# Revit family: SE-SU-600_GENERADO
name_source: partatom
category: Equipos especializados
revit_build: Autodesk Revit 2014 (Build: 20130308_1515(x64)
units: mm (PartAtom-declared; Revit-internal decimal feet)

## types (32) — shared parameters
Depth = 566 mm  [stored 1.85696 ft]
Fabricante = SAMMIC S.L.
Foodservice Equipment Identifier = Sí
Height = 997 mm  [stored 3.271 ft]
Revision Code = 1
URL = https://www.sammic.com
URL Cutsheet = http://www.sammic.com
Width = 740 mm  [stored 2.42782 ft]

## per-type parameters (varying)
| type | Comentarios de tipo | Cycle | FL Amps | HP | Modelo | Phase | Specification by Manufacturer | Volts | Watts | Weight in Pounds |
| Vacuum packing machine SE-604 230-400/50/3N | Floorstanding unit. 40 m³/h. 413+656 mm.

ELECTRICAL DATA:

230V/50Hz/3~ (8.8A) | 50 Hz | 5 A | 3.49 | 1140650 | 3 | Two sealing bars (413+656 mm.)
40 m³/h Busch vacuum pump.
Vacuum controlled by sensor. | 400 V | 2600 W | 319.7 |
| Vacuum packing machine SE-604 208-240V/60/3 | Floorstanding unit. 40 m³/h. 413+656 mm.

ELECTRICAL DATA:

230V/60Hz/3~ (7.4A) | 60 Hz | 7 A | 4.29 | 1140656 | 3 | Two sealing bars (413+656 mm.)
40 m³/h Busch vacuum pump.
Vacuum controlled by sensor. | 208 V | 3200 W | 319.7 |
| Vacuum packing machine SE-604 380/60/3N | Floorstanding unit. 40 m³/h. 413+656 mm. | 60 Hz | 5 A | 3.49 | 1140660 | 3 | Two sealing bars (413+656 mm.)
40 m³/h Busch vacuum pump.
Vacuum controlled by sensor. | 380 V | 2600 W | 319.7 |
| Vacuum packing machine SE-604 CC 230-400/50/3N | Floorstanding unit. 40m³/h. 465+465 mm.

ELECTRICAL DATA:

230V/50Hz/3~ (8.8A) | 50 Hz | 5 A | 3.08 | 1140651 | 3 | Two sealing bars (465+465 mm.)
40 m³/h Busch vacuum pump.
Vacuum controlled by sensor. | 400 V | 2300 W | 319.7 |
| Vacuum packing machine SE-604 CC 208-240V/60/3 | Floorstanding unit. 40m³/h. 465+465 mm.

ELECTRICAL DATA:

230V/60Hz/3~ (7.4A) | 60 Hz | 7 A | 3.89 | 1140657 | 3 | Two sealing bars (465+465 mm.)
40 m³/h Busch vacuum pump.
Vacuum controlled by sensor. | 208 V | 2900 W | 319.7 |
| Vacuum packing machine SE-606 230-400/50/3N | Floorstanding unit. 63 m³/h. 413+656 mm.

ELECTRICAL DATA:

230V/50Hz/3~ (9.5A) | 50 Hz | 6 A | 4.02 | 1140662 | 3 | Two sealing bars (413+656 mm.)
63 m³/h Busch vacuum pump.
Vacuum controlled by sensor. | 400 V | 3000 W | 350.5 |
| Vacuum packing machine SE-606 208-240V/60/3 | Floorstanding unit. 63 m³/h. 413+656 mm.

ELECTRICAL DATA:

230V/60Hz/3~ (8.2A) | 60 Hz | 8 A | 5.23 | 1140668 | 3 | Two sealing bars (413+656 mm.)
63 m³/h Busch vacuum pump.
Vacuum controlled by sensor. | 208 V | 3900 W | 350.5 |
| Vacuum packing machine SE-606 230V/50/1 | Floorstanding unit. 63 m³/h. 413+656 mm. | 50 Hz | 12 A | 4.56 | 1140674 | 1 | Two sealing bars (413+656 mm.)
63 m³/h Busch vacuum pump.
Vacuum controlled by sensor. | 230 V | 3400 W | 350.5 |
| Vacuum packing machine SE-606 CC 230-400/50/3N | Floorstanding unit. 63 m³/h. 465+465 mm.

ELECTRICAL DATA:

230V/50Hz/3~ (9.5A) | 50 Hz | 6 A | 3.62 | 1140663 | 3 | Two sealing bars (465+465 mm.)
63 m³/h Busch vacuum pump.
Vacuum controlled by sensor. | 400 V | 2700 W | 350.5 |
| Vacuum packing machine SE-606 CC 208-240V/60/3 | Floorstanding unit. 63 m³/h. 465+465 mm.

ELECTRICAL DATA:

230V/60Hz/3~ (8.2A) | 60 Hz | 8 A | 4.83 | 1140669 | 3 | Two sealing bars (465+465 mm.)
63 m³/h Busch vacuum pump.
Vacuum controlled by sensor. | 208 V | 3600 W | 350.5 |
| Vacuum packing machine SU-604 230-400/50/3N | Floorstanding unit. 40 m³/h. 413+656 mm.

ELECTRICAL DATA:

230V/50Hz/3~ (8.8A) | 50 Hz | 5 A | 3.49 | 1140811 | 3 | Two sealing bars (413+656 mm.)
40 m³/h Busch vacuum pump.
Vacuum controlled by sensor. | 400 V | 2600 W | 319.7 |
| Vacuum packing machine SU-604P 230-400/50/3N | Floorstanding unit. 40 m³/h. 413+656 mm.

ELECTRICAL DATA:

230V/50Hz/3~ (8.8A) | 50 Hz | 5 A | 3.49 | 1140814 | 3 | Two sealing bars (413+656 mm.)
40 m³/h Busch vacuum pump.
Vacuum controlled by sensor. | 400 V | 2600 W | 319.7 |
| Vacuum packing machine SU-604 208-240/60/3 | Floorstanding unit. 40 m³/h. 413+656 mm.

ELECTRICAL DATA:

230V/60Hz/3~ (7.4A) | 60 Hz | 7 A | 4.29 | 1140823 | 3 | Two sealing bars (413+656 mm.)
40 m³/h Busch vacuum pump.
Vacuum controlled by sensor. | 208 V | 3200 W | 319.7 |
| Vacuum packing machine SU-604P 208-240/60/3 | Floorstanding unit. 40 m³/h. 413+656 mm.

ELECTRICAL DATA:

230V/60Hz/3~ (7.4A) | 60 Hz | 7 A | 4.29 | 1140826 | 3 | Two sealing bars (413+656 mm.)
40 m³/h Busch vacuum pump.
Vacuum controlled by sensor. | 208 V | 3200 W | 319.7 |
| Vacuum packing machine SU-606 230-400/50/3N | Floorstanding unit. 63 m³/h. 413+656 mm.

ELECTRICAL DATA:

230V/50Hz/3~ (9.5A) | 50 Hz | 6 A | 4.02 | 1140835 | 3 | Two sealing bars (413+656 mm.)
63 m³/h Busch vacuum pump.
Vacuum controlled by sensor. | 400 V | 3000 W | 350.5 |
| Vacuum packing machine SU-606P 230-400/50/3N | Floorstanding unit. 63 m³/h. 413+656 mm.

ELECTRICAL DATA:

230V/50Hz/3~ (9.5A) | 50 Hz | 6 A | 4.02 | 1140838 | 3 | Two sealing bars (413+656 mm.)
63 m³/h Busch vacuum pump.
Vacuum controlled by sensor. | 400 V | 3000 W | 350.5 |
| Vacuum packing machine SU-606+ 230-400/50/3N | Floorstanding unit. 63 m³/h. 413+656 mm.

ELECTRICAL DATA:

230V/50Hz/3~ (9.5A) | 50 Hz | 6 A | 4.02 | 1140839 | 3 | Two sealing bars (413+656 mm.)
63 m³/h Busch vacuum pump.
Vacuum controlled by sensor. | 400 V | 3000 W | 350.5 |
| Vacuum packing machine SU-606P+ 230-400/50/3N | Floorstanding unit. 63 m³/h. 413+656 mm.

ELECTRICAL DATA:

230V/50Hz/3~ (9.5A) | 50 Hz | 6 A | 4.02 | 1140840 | 3 | Two sealing bars (413+656 mm.)
63 m³/h Busch vacuum pump.
Vacuum controlled by sensor. | 400 V | 3000 W | 350.5 |
| Vacuum packing machine SU-606 208-240/60/3 | Floorstanding unit. 63 m³/h. 413+656 mm.

ELECTRICAL DATA:

230V/60Hz/3~ (8.2A) | 60 Hz | 8 A | 5.23 | 1140855 | 3 | Two sealing bars (413+656 mm.)
63 m³/h Busch vacuum pump.
Vacuum controlled by sensor. | 208 V | 3900 W | 350.5 |
| Vacuum packing machine SU-606P 208-240/60/3 | Floorstanding unit. 63 m³/h. 413+656 mm.

ELECTRICAL DATA:

230V/60Hz/3~ (8.2A) | 60 Hz | 8 A | 5.23 | 1140858 | 3 | Two sealing bars (413+656 mm.)
63 m³/h Busch vacuum pump.
Vacuum controlled by sensor. | 208 V | 3900 W | 350.5 |
| Vacuum packing machine SU-606+ 208-240/60/3 | Floorstanding unit. 63 m³/h. 413+656 mm.

ELECTRICAL DATA:

230V/60Hz/3~ (8.2A) | 60 Hz | 8 A | 5.23 | 1140859 | 3 | Two sealing bars (413+656 mm.)
63 m³/h Busch vacuum pump.
Vacuum controlled by sensor. | 208 V | 3900 W | 350.5 |
| Vacuum packing machine SU-606P+ 208-240/60/3 | Floorstanding unit. 63 m³/h. 413+656 mm.

ELECTRICAL DATA:

230V/60Hz/3~ (8.2A) | 60 Hz | 8 A | 5.23 | 1140860 | 3 | Two sealing bars (413+656 mm.)
63 m³/h Busch vacuum pump.
Vacuum controlled by sensor. | 208 V | 3900 W | 350.5 |
| Vacuum packing machine SU-604 CC 230-400/50/3N | Floorstanding unit. 40m³/h. 465+465 mm.

ELECTRICAL DATA:

230V/50Hz/3~ (8.8A) | 50 Hz | 5 A | 3.08 | 1140817 | 3 | Two sealing bars (465+465 mm.)
40 m³/h Busch vacuum pump.
Vacuum controlled by sensor. | 400 V | 2300 W | 319.7 |
| Vacuum packing machine SU-604P CC 230-400/50/3N | Floorstanding unit. 40m³/h. 465+465 mm.

ELECTRICAL DATA:

230V/50Hz/3~ (8.8A) | 50 Hz | 5 A | 3.08 | 1140820 | 3 | Two sealing bars (465+465 mm.)
40 m³/h Busch vacuum pump.
Vacuum controlled by sensor. | 400 V | 2300 W | 319.7 |
| Vacuum packing machine SU-604 CC 208-240/60/3 | Floorstanding unit. 40m³/h. 465+465 mm.

ELECTRICAL DATA:

230V/60Hz/3~ (7.4A) | 60 Hz | 7 A | 3.89 | 1140829 | 3 | Two sealing bars (465+465 mm.)
40 m³/h Busch vacuum pump.
Vacuum controlled by sensor. | 208 V | 2900 W | 319.7 |
| Vacuum packing machine SU-606 CC 230-400/50/3N | Floorstanding unit. 63 m³/h. 465+465 mm.

ELECTRICAL DATA:

230V/50Hz/3~ (9.5A) | 50 Hz | 6 A | 3.62 | 1140845 | 3 | Two sealing bars (465+465 mm.)
63 m³/h Busch vacuum pump.
Vacuum controlled by sensor. | 400 V | 2700 W | 350.5 |
| Vacuum packing machine SU-606P CC 230-400/50/3N | Floorstanding unit. 63 m³/h. 465+465 mm.

ELECTRICAL DATA:

230V/50Hz/3~ (9.5A) | 50 Hz | 6 A | 3.62 | 1140848 | 3 | Two sealing bars (465+465 mm.)
63 m³/h Busch vacuum pump.
Vacuum controlled by sensor. | 400 V | 2700 W | 350.5 |
| Vacuum packing machine SU-606+ CC 230-400/50/3N | Floorstanding unit. 63 m³/h. 465+465 mm.

ELECTRICAL DATA:

230V/50Hz/3~ (9.5A) | 50 Hz | 6 A | 3.62 | 1140849 | 3 | Two sealing bars (465+465 mm.)
63 m³/h Busch vacuum pump.
Vacuum controlled by sensor. | 400 V | 2700 W | 350.5 |
| Vacuum packing machine SU-606P+ CC 230-400/50/3N | Floorstanding unit. 63 m³/h. 465+465 mm.

ELECTRICAL DATA:

230V/50Hz/3~ (9.5A) | 50 Hz | 6 A | 3.62 | 1140850 | 3 | Two sealing bars (465+465 mm.)
63 m³/h Busch vacuum pump.
Vacuum controlled by sensor. | 400 V | 2700 W | 350.5 |
| Vacuum packing machine SU-606 CC 208-240/60/3 | Floorstanding unit. 63 m³/h. 465+465 mm.

ELECTRICAL DATA:

230V/60Hz/3~ (8.2A) | 60 Hz | 8 A | 4.83 | 1140865 | 3 | Two sealing bars (465+465 mm.)
63 m³/h Busch vacuum pump.
Vacuum controlled by sensor. | 208 V | 3600 W | 350.5 |
| Vacuum packing machine SU-606+ CC 208-240/60/3 | Floorstanding unit. 63 m³/h. 465+465 mm.

ELECTRICAL DATA:

230V/60Hz/3~ (8.2A) | 60 Hz | 8 A | 4.83 | 1140869 | 3 | Two sealing bars (465+465 mm.)
63 m³/h Busch vacuum pump.
Vacuum controlled by sensor. | 208 V | 3600 W | 350.5 |
| Vacuum packing machine SU-606P+ CC 208-240/60/3 | Floorstanding unit. 63 m³/h. 465+465 mm.

ELECTRICAL DATA:

230V/60Hz/3~ (8.2A) | 60 Hz | 8 A | 4.83 | 1140870 | 3 | Two sealing bars (465+465 mm.)
63 m³/h Busch vacuum pump.
Vacuum controlled by sensor. | 208 V | 3600 W | 350.5 |

note: column(s) folded — value = type name in every type: Descripción

note: [stored X ft] marks values corroborated as IEEE doubles in the binary element streams (Revit-internal decimal feet)
